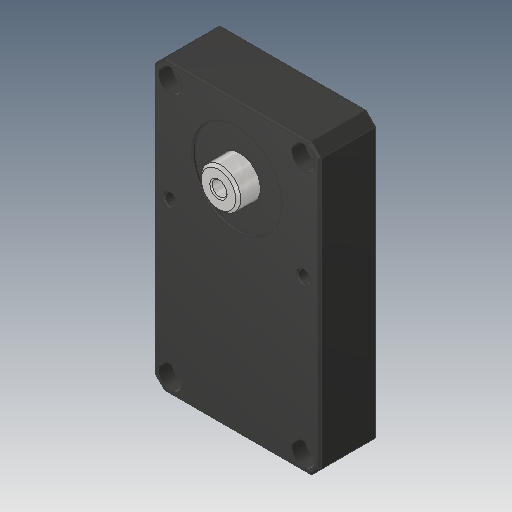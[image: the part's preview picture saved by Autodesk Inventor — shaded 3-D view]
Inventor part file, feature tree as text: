
AUTODESK INVENTOR PART (.ipt)
format: ipt  version: 2019.4 (Build 234330000, 330)  size: 222,720 bytes
history: native  units: mm
features: sketch x5, extrude x3, chamfer x2, other x1, hole x1, revolve x1
ambient origin geometry x8: Origin, YZ Plane, XZ Plane, XY Plane, X Axis, Y Axis, Z Axis, Center Point
bodies: Body1 (feature_tree)
feature tree (13):
  other  "ソリッド1"
  extrude  "押し出し1"  Depth=2.0mm
  hole  "穴1"  [1 undecoded]
  extrude  "押し出し2"  Depth=2.0mm
  extrude  "押し出し3"  Depth=2.0mm
  chamfer  "面取り1"  Distance=2.0mm
  chamfer  "面取り2"  Distance=2.0mm
  revolve  "回転1"
  sketch  "スケッチ1"
  sketch  "スケッチ2"
  sketch  "スケッチ3"
  sketch  "スケッチ4"
  sketch  "スケッチ6"
note: 1 required parameter value undecoded (feature->parameter linkage not recoverable at this tier; creation-order binding heuristic only, values carry confidence <= 0.55)
